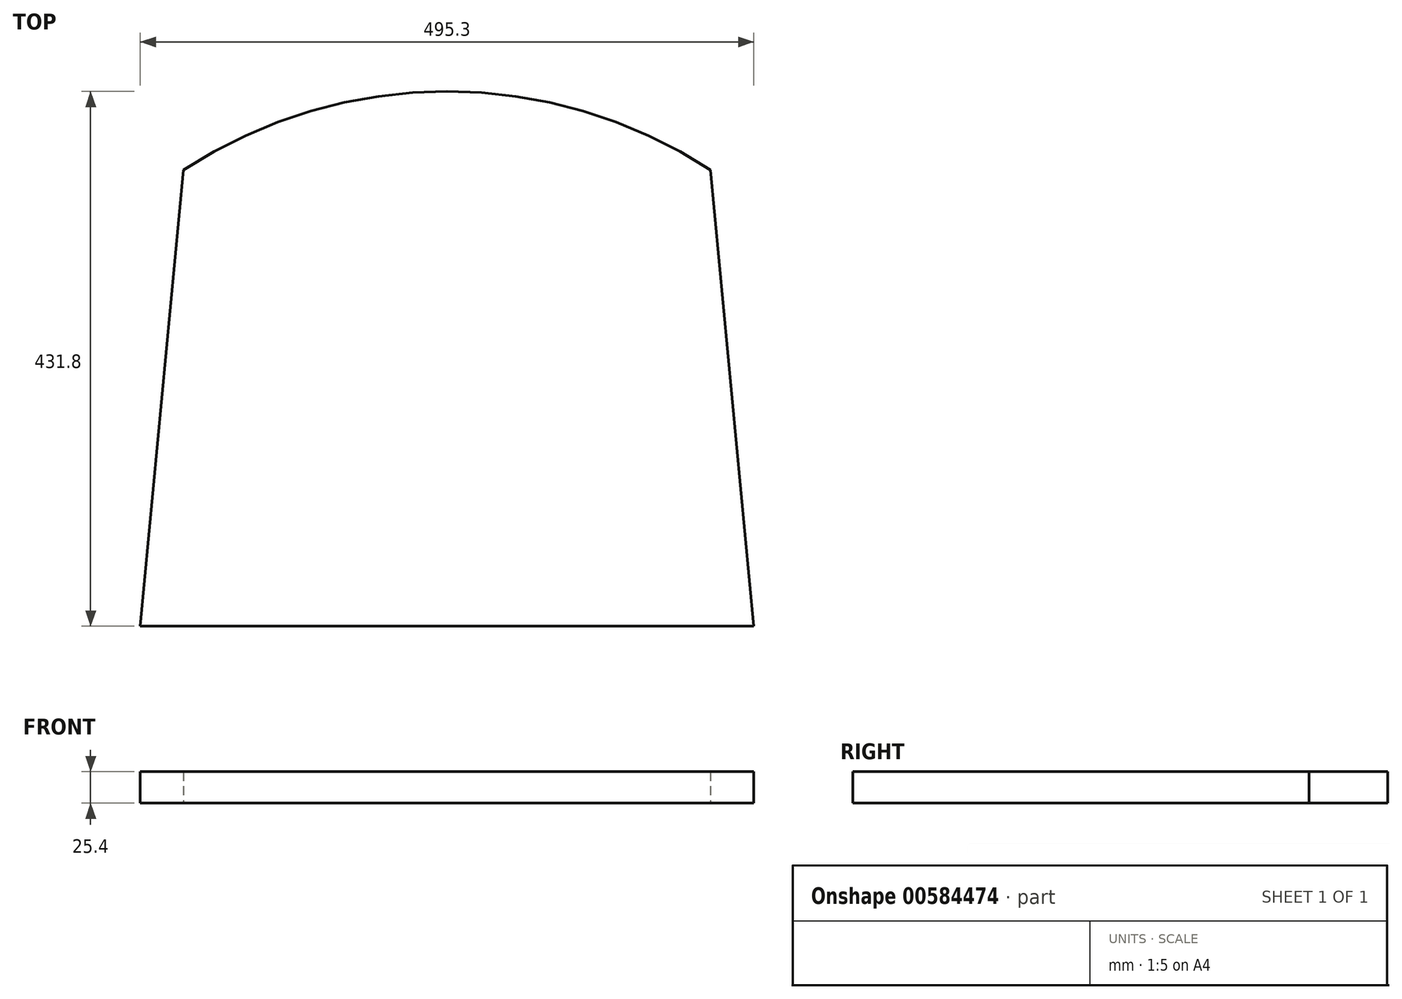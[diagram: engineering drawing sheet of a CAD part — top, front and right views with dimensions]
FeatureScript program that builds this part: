
annotation { "Feature Type Name" : "Feature", "Feature Type Description" : "" }
export const myFeature = defineFeature(function(context is Context, id is Id, definition is map)
    precondition{}
    {
        {
            var Q0;
            Q0=qCreatedBy(makeId("Top.planeOp"),FACE);
            var sketch = newSketch(context, id + "F0", { "sketchPlane" : qUnion([Q0])});
            skLineSegment(sketch, "E0.bottom", {"start": v(247.65, -420.9) * mm, "end": v(-247.65, -420.9) * mm});
            skLineSegment(sketch, "E0.left", {"start": v(247.65, -420.9) * mm, "end": v(212.72, -52.6) * mm});
            skLineSegment(sketch, "E0.right", {"start": v(-247.65, -420.9) * mm, "end": v(-212.72, -52.6) * mm});
            skArc(sketch, "E1", {"start": v(212.73, -52.6) * mm, "mid": v(0, 10.9) * mm, "end": v(-212.73, -52.6) * mm});
            skLineSegment(sketch, "E2", {"start": v(-212.73, -52.6) * mm, "end": v(212.73, -52.6) * mm, "construction": true});
            skSolve(sketch);
        }
        {
            var Q0;
            Q0=makeQuery(id+"F0.imprint","IMPRINT",FACE,{"disambiguationData":[TD([[makeQuery(id+"F0.imprint","IMPRINT",EDGE,{"derivedFrom":sQuery(id+"F0.wireOp",EDGE,"E0.bottom")}),-1.0]])]});
            extrude(context, id + "F1", {"entities" : qUnion([Q0]), "depth" : 25.4 * mm, "offsetDistance" : 25.4 * mm});
        }
    });
